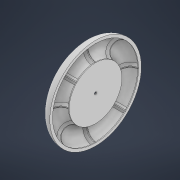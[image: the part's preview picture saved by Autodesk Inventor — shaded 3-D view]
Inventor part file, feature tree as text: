
AUTODESK INVENTOR PART (.ipt)
format: ipt  version: 2021 (Build 250183000, 183)  size: 1,576,960 bytes
history: native  units: mm
features: sketch x5, extrude x3, revolve x2, other x1, chamfer x1
ambient origin geometry x8: Origin, YZ Plane, XZ Plane, XY Plane, X Axis, Y Axis, Z Axis, Center Point
bodies: Body1 (feature_tree)
feature tree (12):
  other  "Твердое тело1"
  revolve  "Вращение1"
  extrude  "Выдавливание1"  TaperAngle=90.0deg  [1 undecoded]
  extrude  "Выдавливание2"  Depth=80.0mm TaperAngle=360.0deg
  revolve  "Вращение2"
  extrude  "Выдавливание3"  TaperAngle=0.0deg  [1 undecoded]
  chamfer  "Фаска1"  Distance=1.5mm
  sketch  "Эскиз1"
  sketch  "Эскиз2"
  sketch  "Эскиз3"
  sketch  "Эскиз4"
  sketch  "Эскиз5"
note: 2 required parameter values undecoded (feature->parameter linkage not recoverable at this tier; creation-order binding heuristic only, values carry confidence <= 0.55)
